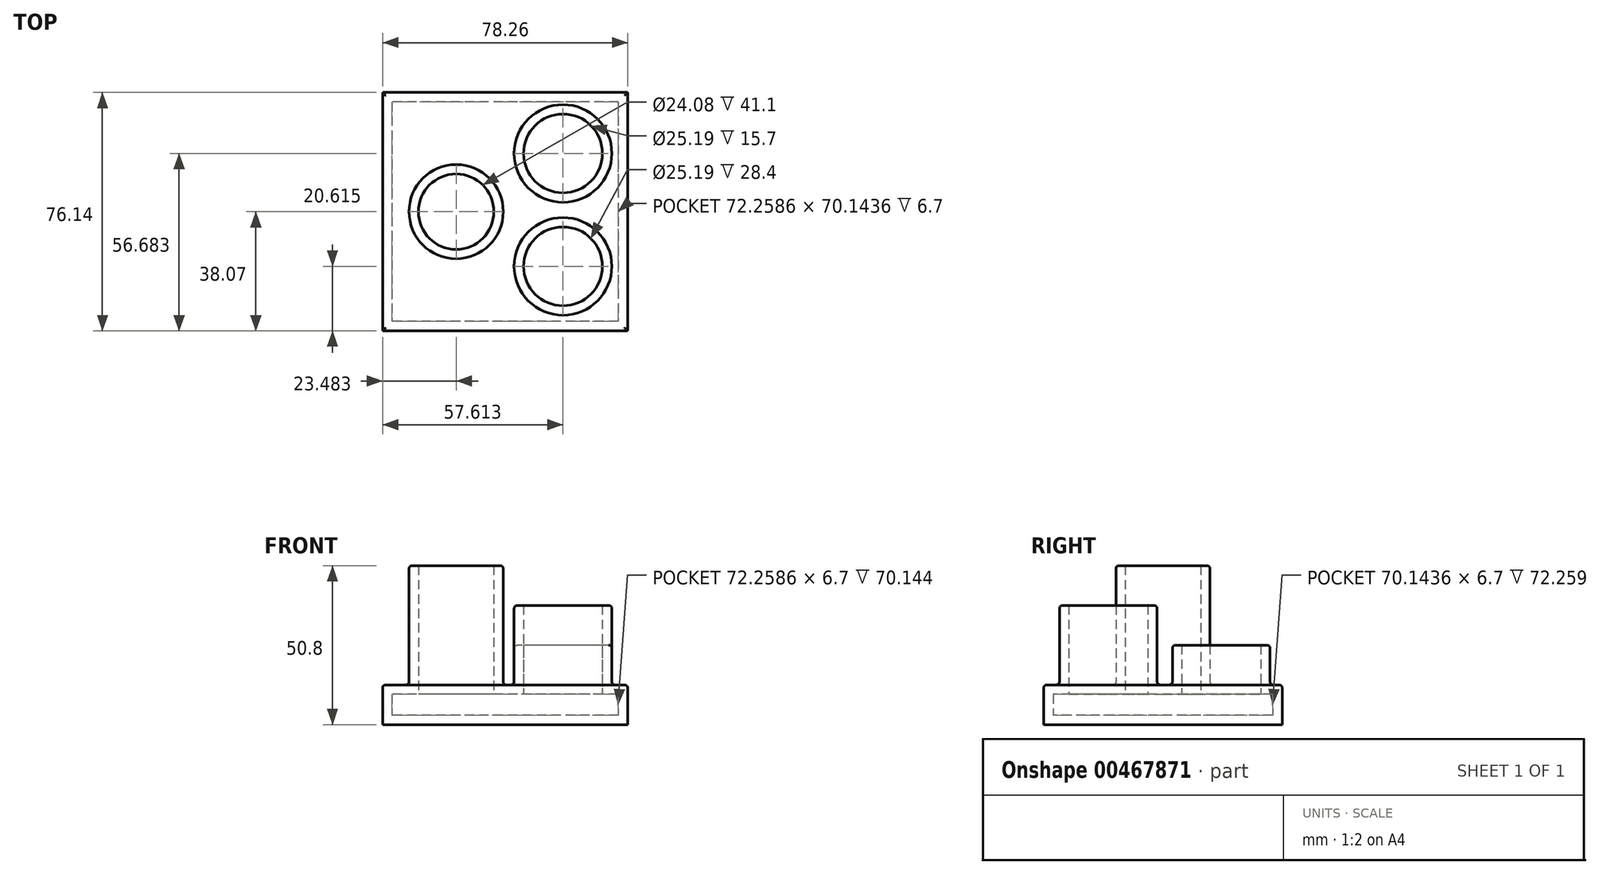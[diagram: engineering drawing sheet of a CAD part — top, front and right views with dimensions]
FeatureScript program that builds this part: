
annotation { "Feature Type Name" : "Feature", "Feature Type Description" : "" }
export const myFeature = defineFeature(function(context is Context, id is Id, definition is map)
    precondition{}
    {
        {
            var Q0;
            Q0=qCreatedBy(makeId("Top.planeOp"),FACE);
            var sketch = newSketch(context, id + "F0", { "sketchPlane" : qUnion([Q0])});
            skLineSegment(sketch, "E0.bottom", {"start": v(39.13, 38.07) * mm, "end": v(-39.13, 38.07) * mm});
            skLineSegment(sketch, "E0.top", {"start": v(39.13, -38.07) * mm, "end": v(-39.13, -38.07) * mm});
            skLineSegment(sketch, "E0.left", {"start": v(39.13, 38.07) * mm, "end": v(39.13, -38.07) * mm});
            skLineSegment(sketch, "E0.right", {"start": v(-39.13, 38.07) * mm, "end": v(-39.13, -38.07) * mm});
            skPoint(sketch, "E0.middle", {"position": v(0, 0) * mm});
            skCircle(sketch, "E1", {"center": v(-15.65, 0) * mm, "radius": 15.04 * mm});
            skCircle(sketch, "E2", {"center": v(18.48, 18.61) * mm, "radius": 15.6 * mm});
            skCircle(sketch, "E3", {"center": v(18.48, -17.45) * mm, "radius": 15.6 * mm});
            skSolve(sketch);
        }
        {
            var Q0;
            Q0=makeQuery(id+"F0.imprint","IMPRINT",FACE,{"disambiguationData":[TD([[makeQuery(id+"F0.imprint","IMPRINT",EDGE,{"derivedFrom":sQuery(id+"F0.wireOp",EDGE,"E0.bottom")}),1.0]])]});
            var sketch = newSketch(context, id + "F1", { "sketchPlane" : qUnion([Q0])});
            skSolve(sketch);
        }
        {
            var Q0;
            Q0 = qSketchRegion(id + "F1", true);
            var Q1;
            Q1=makeQuery(id+"F0.imprint","IMPRINT",FACE,{"disambiguationData":[TD([[makeQuery(id+"F0.imprint","IMPRINT",EDGE,{"derivedFrom":sQuery(id+"F0.wireOp",EDGE,"E0.bottom")}),1.0]])]});
            extrude(context, id + "F2", {"entities" : qUnion([Q0, Q1]), "depth" : 12.7 * mm});
        }
        {
            var Q0;
            Q0=makeQuery(id+"F1.imprint","IMPRINT",FACE,{"disambiguationData":[TD([[makeQuery(id+"F1.imprint","IMPRINT",EDGE,{"derivedFrom":makeQuery(id+"F0.imprint","IMPRINT",EDGE,{"derivedFrom":sQuery(id+"F0.wireOp",EDGE,"E1")})}),1.0]])]});
            var Q1;
            Q1=makeQuery(id+"F1.imprint","IMPRINT",FACE,{"disambiguationData":[TD([[makeQuery(id+"F1.imprint","IMPRINT",EDGE,{"derivedFrom":makeQuery(id+"F0.imprint","IMPRINT",EDGE,{"derivedFrom":sQuery(id+"F0.wireOp",EDGE,"E2")})}),1.0]])]});
            var Q2;
            Q2=makeQuery(id+"F1.imprint","IMPRINT",FACE,{"disambiguationData":[TD([[makeQuery(id+"F1.imprint","IMPRINT",EDGE,{"derivedFrom":makeQuery(id+"F0.imprint","IMPRINT",EDGE,{"derivedFrom":sQuery(id+"F0.wireOp",EDGE,"E3")})}),1.0]])]});
            extrude(context, id + "F3", {"entities" : qUnion([Q0, Q1, Q2]), "operationType" : NewBodyOperationType.ADD, "depth" : 25.4 * mm});
        }
        {
            var Q0;
            Q0=makeQuery(id+"F3.opExtrude","CAP_FACE",FACE,{"disambiguationData":[OSD([sQuery(id+"F0.wireOp",EDGE,"E1")])],"isStart":false});
            extrude(context, id + "F4", {"entities" : qUnion([Q0]), "operationType" : NewBodyOperationType.ADD, "depth" : 25.4 * mm});
        }
        {
            var Q0;
            Q0=makeQuery(id+"F3.opExtrude","CAP_FACE",FACE,{"disambiguationData":[OSD([sQuery(id+"F0.wireOp",EDGE,"E3")])],"isStart":false});
            extrude(context, id + "F5", {"entities" : qUnion([Q0]), "operationType" : NewBodyOperationType.ADD, "depth" : 12.7 * mm});
        }
        {
            var Q0;
            Q0=makeQuery(id+"F4.opExtrude","CAP_FACE",FACE,{"disambiguationData":[OSD([sQuery(id+"F0.wireOp",EDGE,"E1")])],"isStart":false});
            var Q1;
            Q1=makeQuery(id+"F5.opExtrude","CAP_FACE",FACE,{"disambiguationData":[OSD([sQuery(id+"F0.wireOp",EDGE,"E3")])],"isStart":false});
            var Q2;
            Q2=makeQuery(id+"F3.opExtrude","CAP_FACE",FACE,{"disambiguationData":[OSD([sQuery(id+"F0.wireOp",EDGE,"E2")])],"isStart":false});
            shell(context, id + "F6", {"entities" : qUnion([Q0, Q1, Q2]), "thickness" : 3 * mm});
        }
        {
            var Q0;
            {var subQ0=sQuery(id+"F0.wireOp",EDGE,"E1");Q0=makeQuery(id+"F4.boolean.opBoolean","MERGE",FACE,{"derivedFrom":[makeQuery(id+"F3.opExtrude","SWEPT_FACE",FACE,{"disambiguationData":[OSD([subQ0])]}),makeQuery(id+"F4.opExtrude","SWEPT_FACE",FACE,{"disambiguationData":[OSD([subQ0])]})]});}
            var Q1;
            {var subQ0=sQuery(id+"F0.wireOp",EDGE,"E3");Q1=makeQuery(id+"F5.boolean.opBoolean","MERGE",FACE,{"derivedFrom":[makeQuery(id+"F3.opExtrude","SWEPT_FACE",FACE,{"disambiguationData":[OSD([subQ0])]}),makeQuery(id+"F5.opExtrude","SWEPT_FACE",FACE,{"disambiguationData":[OSD([subQ0])]})]});}
            var Q2;
            Q2=makeQuery(id+"F3.opExtrude","SWEPT_FACE",FACE,{"disambiguationData":[OSD([sQuery(id+"F0.wireOp",EDGE,"E2")])]});
            var Q3;
            Q3=makeQuery(id+"F2.opExtrude","CAP_FACE",FACE,{"disambiguationData":[OSD([sQuery(id+"F0.wireOp",EDGE,"E0.bottom"),sQuery(id+"F0.wireOp",EDGE,"E0.top"),sQuery(id+"F0.wireOp",EDGE,"E0.left"),sQuery(id+"F0.wireOp",EDGE,"E0.right"),sQuery(id+"F0.wireOp",EDGE,"E1"),sQuery(id+"F0.wireOp",EDGE,"E2"),sQuery(id+"F0.wireOp",EDGE,"E3")])],"isStart":false});
            fillet(context, id + "F7", {"entities" : qUnion([Q0, Q1, Q2, Q3]), "radius" : 1 * mm, "tangentPropagation" : true, "allowEdgeOverflow" : false});
        }
    });
